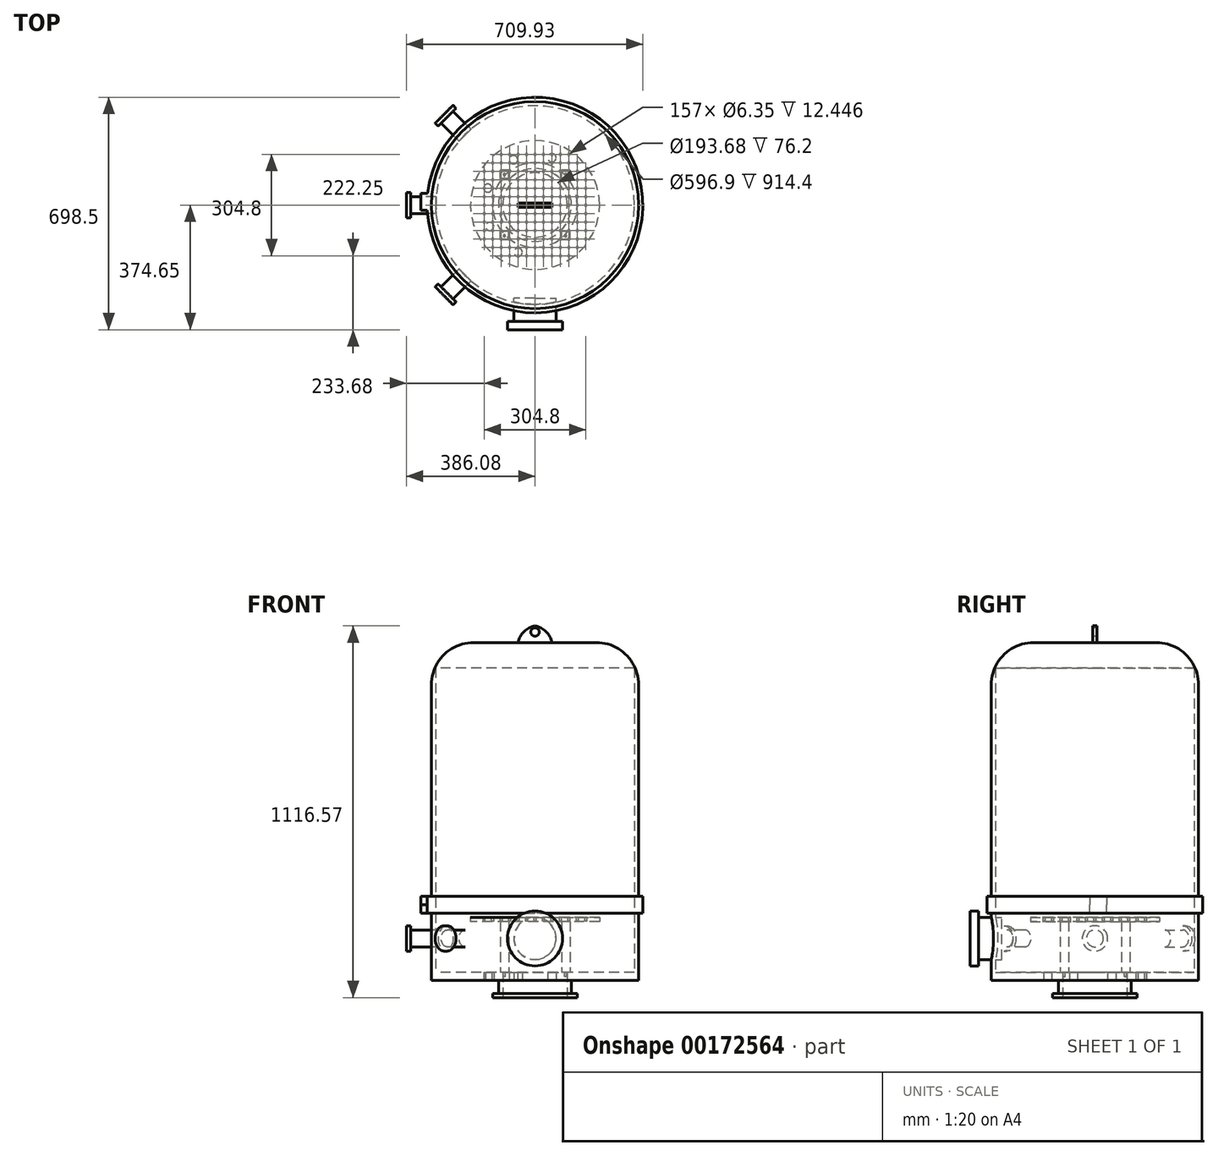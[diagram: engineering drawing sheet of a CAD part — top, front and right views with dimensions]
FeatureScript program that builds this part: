
annotation { "Feature Type Name" : "Feature", "Feature Type Description" : "" }
export const myFeature = defineFeature(function(context is Context, id is Id, definition is map)
    precondition{}
    {
        {
            var Q0;
            Q0=qCreatedBy(makeId("Top.planeOp"),FACE);
            var sketch = newSketch(context, id + "F0", { "sketchPlane" : qUnion([Q0])});
            skCircle(sketch, "E0", {"center": v(0, 0) * mm, "radius": 311.15 * mm});
            skCircle(sketch, "E1", {"center": v(0, 0) * mm, "radius": 298.45 * mm});
            skSolve(sketch);
        }
        {
            var Q0;
            Q0=makeQuery(id+"F0.imprint","IMPRINT",FACE,{"disambiguationData":[TD([[makeQuery(id+"F0.imprint","IMPRINT",EDGE,{"derivedFrom":sQuery(id+"F0.wireOp",EDGE,"E0")}),1.0]])]});
            extrude(context, id + "F1", {"entities" : qUnion([Q0]), "depth" : 177.8 * mm});
        }
        {
            var Q0;
            Q0=makeQuery(id+"F1.opExtrude","CAP_FACE",FACE,{"disambiguationData":[OSD([sQuery(id+"F0.wireOp",EDGE,"E0"),sQuery(id+"F0.wireOp",EDGE,"E1")])],"isStart":false});
            var sketch = newSketch(context, id + "F2", { "sketchPlane" : qUnion([Q0])});
            skCircle(sketch, "E2", {"center": v(0, 0) * mm, "radius": 323.85 * mm});
            skCircle(sketch, "E3", {"center": v(0, 0) * mm, "radius": 298.45 * mm});
            skSolve(sketch);
        }
        {
            var Q0;
            Q0 = qSketchRegion(id + "F2", true);
            extrude(context, id + "F3", {"entities" : qUnion([Q0]), "operationType" : NewBodyOperationType.ADD, "depth" : 25.4 * mm});
        }
        {
            var Q0;
            Q0=qCreatedBy(makeId("Front.planeOp"),FACE);
            cPlane(context, id + "F4", {"entities" : qUnion([Q0]), "cplaneType" : CPlaneType.OFFSET, "offset" : 304.8 * mm, "width" : 152.4 * mm, "height" : 152.4 * mm});
        }
        {
            var Q0;
            Q0=qCreatedBy(id+"F4.planeOp",FACE);
            var sketch = newSketch(context, id + "F5", { "sketchPlane" : qUnion([Q0])});
            skLineSegment(sketch, "E4", {"start": v(0, 0) * mm, "end": v(0, 203.2) * mm, "construction": true});
            skLineSegment(sketch, "E5", {"start": v(0, 101.6) * mm, "end": v(254, 101.6) * mm, "construction": true});
            skPoint(sketch, "E5.endSnap0", {"position": v(0, 101.6) * mm});
            skLineSegment(sketch, "E6", {"start": v(254, 101.6) * mm, "end": v(-254, 101.6) * mm, "construction": true});
            skCircle(sketch, "E7", {"center": v(0, 101.6) * mm, "radius": 63.5 * mm});
            skSolve(sketch);
        }
        {
            var Q0;
            Q0 = qSketchRegion(id + "F5", true);
            extrude(context, id + "F6", {"entities" : qUnion([Q0]), "operationType" : NewBodyOperationType.ADD, "depth" : 44.45 * mm, "hasSecondDirection" : true, "secondDirectionOppositeDirection" : true, "secondDirectionDepth" : 25.4 * mm});
        }
        {
            var Q0;
            Q0=makeQuery(id+"F6.opExtrude","CAP_FACE",FACE,{"disambiguationData":[OSD([sQuery(id+"F5.wireOp",EDGE,"E7")])],"isStart":false});
            var sketch = newSketch(context, id + "F7", { "sketchPlane" : qUnion([Q0])});
            skCircle(sketch, "E8", {"center": v(0, 101.6) * mm, "radius": 82.55 * mm});
            skSolve(sketch);
        }
        {
            var Q0;
            Q0 = qSketchRegion(id + "F7", true);
            extrude(context, id + "F8", {"entities" : qUnion([Q0]), "operationType" : NewBodyOperationType.ADD, "depth" : 25.4 * mm});
        }
        {
            var Q0;
            Q0=qCreatedBy(makeId("Right.planeOp"),FACE);
            cPlane(context, id + "F9", {"entities" : qUnion([Q0]), "cplaneType" : CPlaneType.OFFSET, "offset" : 304.8 * mm, "oppositeDirection" : true, "width" : 152.4 * mm, "height" : 152.4 * mm});
        }
        {
            var Q0;
            Q0=qCreatedBy(id+"F9.planeOp",FACE);
            var sketch = newSketch(context, id + "F10", { "sketchPlane" : qUnion([Q0])});
            skLineSegment(sketch, "E9", {"start": v(0, 0) * mm, "end": v(0, 203.2) * mm, "construction": true});
            skLineSegment(sketch, "E10", {"start": v(0, 101.6) * mm, "end": v(-254, 101.6) * mm, "construction": true});
            skPoint(sketch, "E10.endSnap0", {"position": v(0, 101.6) * mm});
            skLineSegment(sketch, "E11", {"start": v(-254, 101.6) * mm, "end": v(254, 101.6) * mm, "construction": true});
            skCircle(sketch, "E12", {"center": v(0, 101.6) * mm, "radius": 25.4 * mm});
            skSolve(sketch);
        }
        {
            var Q0;
            Q0 = qSketchRegion(id + "F10", true);
            extrude(context, id + "F11", {"entities" : qUnion([Q0]), "depth" : 7.62 * mm, "hasSecondDirection" : true, "secondDirectionOppositeDirection" : true, "secondDirectionDepth" : 68.58 * mm});
        }
        {
            var Q0;
            Q0=makeQuery(id+"F11.opExtrude","CAP_FACE",FACE,{"disambiguationData":[OSD([sQuery(id+"F10.wireOp",EDGE,"E12")])],"isStart":true});
            var sketch = newSketch(context, id + "F12", { "sketchPlane" : qUnion([Q0])});
            skCircle(sketch, "E13", {"center": v(0, 101.6) * mm, "radius": 38.1 * mm});
            skSolve(sketch);
        }
        {
            var Q0;
            Q0 = qSketchRegion(id + "F12", true);
            extrude(context, id + "F13", {"entities" : qUnion([Q0]), "operationType" : NewBodyOperationType.ADD, "depth" : 12.7 * mm});
        }
        {
            var Q0;
            Q0=makeQuery(id+"F11.opExtrude","SWEPT_BODY",BODY,{"disambiguationData":[OSD([sQuery(id+"F10.wireOp",EDGE,"E12")])]});
            var Q1;
            Q1=makeQuery(id+"F1.opExtrude","CAP_EDGE",EDGE,{"disambiguationData":[OSD([sQuery(id+"F0.wireOp",EDGE,"E0")])],"isStart":true});
            circularPattern(context, id + "F14", {"entities" : qUnion([Q0]), "axis" : qUnion([Q1]), "angle" : 45 * degree, "instanceCount" : 2, "oppositeDirection" : true});
        }
        {
            var Q0;
            Q0=makeQuery(id+"F11.opExtrude","SWEPT_BODY",BODY,{"disambiguationData":[OSD([sQuery(id+"F10.wireOp",EDGE,"E12")])]});
            var Q1;
            Q1=makeQuery(id+"F1.opExtrude","CAP_EDGE",EDGE,{"disambiguationData":[OSD([sQuery(id+"F0.wireOp",EDGE,"E0")])],"isStart":true});
            circularPattern(context, id + "F15", {"entities" : qUnion([Q0]), "axis" : qUnion([Q1]), "angle" : 45 * degree, "instanceCount" : 2});
        }
        {
            var Q0;
            Q0=makeQuery(id+"F3.opExtrude","CAP_FACE",FACE,{"disambiguationData":[OSD([sQuery(id+"F2.wireOp",EDGE,"E2"),sQuery(id+"F2.wireOp",EDGE,"E3")])],"isStart":false});
            var sketch = newSketch(context, id + "F16", { "sketchPlane" : qUnion([Q0])});
            skCircle(sketch, "E14", {"center": v(0, 0) * mm, "radius": 323.85 * mm});
            skCircle(sketch, "E15", {"center": v(0, 0) * mm, "radius": 298.45 * mm});
            skSolve(sketch);
        }
        {
            var Q0;
            Q0 = qSketchRegion(id + "F16", true);
            extrude(context, id + "F17", {"entities" : qUnion([Q0]), "depth" : 25.4 * mm});
        }
        {
            var Q0;
            Q0=makeQuery(id+"F17.opExtrude","CAP_FACE",FACE,{"disambiguationData":[OSD([sQuery(id+"F16.wireOp",EDGE,"E14"),sQuery(id+"F16.wireOp",EDGE,"E15")])],"isStart":false});
            var sketch = newSketch(context, id + "F18", { "sketchPlane" : qUnion([Q0])});
            skCircle(sketch, "E16", {"center": v(0, 0) * mm, "radius": 298.45 * mm});
            skCircle(sketch, "E17", {"center": v(0, 0) * mm, "radius": 311.15 * mm});
            skSolve(sketch);
        }
        {
            var Q0;
            Q0=makeQuery(id+"F18.imprint","IMPRINT",FACE,{"disambiguationData":[TD([[makeQuery(id+"F18.imprint","IMPRINT",EDGE,{"derivedFrom":sQuery(id+"F18.wireOp",EDGE,"E16")}),-1.0]])]});
            extrude(context, id + "F19", {"entities" : qUnion([Q0]), "operationType" : NewBodyOperationType.ADD, "depth" : 685.8 * mm});
        }
        {
            var Q0;
            Q0=makeQuery(id+"F19.opExtrude","CAP_FACE",FACE,{"disambiguationData":[OSD([sQuery(id+"F18.wireOp",EDGE,"0rSFMXk0-wgXn-WOUg-yUmk-ADJ3Ojx0R6x5"),sQuery(id+"F18.wireOp",EDGE,"E16")])],"isStart":false});
            var sketch = newSketch(context, id + "F20", { "sketchPlane" : qUnion([Q0])});
            skCircle(sketch, "E18", {"center": v(0, 0) * mm, "radius": 311.15 * mm});
            skSolve(sketch);
        }
        {
            var Q0;
            Q0 = qSketchRegion(id + "F20", true);
            extrude(context, id + "F21", {"entities" : qUnion([Q0]), "operationType" : NewBodyOperationType.ADD, "depth" : 76.2 * mm});
        }
        {
            var Q0;
            Q0=makeQuery(id+"F1.opExtrude","CAP_FACE",FACE,{"disambiguationData":[OSD([sQuery(id+"F0.wireOp",EDGE,"E0")])],"isStart":true});
            var sketch = newSketch(context, id + "F22", { "sketchPlane" : qUnion([Q0])});
            skCircle(sketch, "E19", {"center": v(0, 0) * mm, "radius": 109.54 * mm});
            skSolve(sketch);
        }
        {
            var Q0;
            Q0 = qSketchRegion(id + "F22", true);
            extrude(context, id + "F23", {"entities" : qUnion([Q0]), "operationType" : NewBodyOperationType.ADD, "depth" : 63.5 * mm});
        }
        {
            var Q0;
            Q0=makeQuery(id+"F1.opExtrude","CAP_FACE",FACE,{"disambiguationData":[OSD([sQuery(id+"F0.wireOp",EDGE,"E0")])],"isStart":true});
            var sketch = newSketch(context, id + "F24", { "sketchPlane" : qUnion([Q0])});
            skLineSegment(sketch, "E20", {"start": v(50.72, -141.82) * mm, "end": v(0, 0) * mm, "construction": true});
            skCircle(sketch, "E21", {"center": v(50.72, -141.82) * mm, "radius": 12.5 * mm});
            skCircle(sketch, "E22.1.0", {"center": v(-64.42, -136.14) * mm, "radius": 12.5 * mm});
            skCircle(sketch, "E22.2.0", {"center": v(-141.82, -50.72) * mm, "radius": 12.5 * mm});
            skCircle(sketch, "E22.3.0", {"center": v(-136.14, 64.42) * mm, "radius": 12.5 * mm});
            skCircle(sketch, "E22.4.0", {"center": v(-50.72, 141.82) * mm, "radius": 12.5 * mm});
            skPoint(sketch, "E22.center", {"position": v(0, 0) * mm});
            skLineSegment(sketch, "E22.anchor2", {"start": v(-50.72, 141.82) * mm, "end": v(0, 0) * mm, "construction": true});
            skCircle(sketch, "E23", {"center": v(0, 0) * mm, "radius": 96.84 * mm});
            skSolve(sketch);
        }
        {
            var Q0;
            Q0=makeQuery(id+"F21.opExtrude","CAP_FACE",FACE,{"disambiguationData":[OSD([sQuery(id+"F20.wireOp",EDGE,"E18")])],"isStart":false});
            var sketch = newSketch(context, id + "F25", { "sketchPlane" : qUnion([Q0])});
            skPoint(sketch, "E24.0.midPoint", {"position": v(0, 0) * mm});
            skLineSegment(sketch, "E25.bottom", {"start": v(50.8, -6.35) * mm, "end": v(-50.8, -6.35) * mm});
            skLineSegment(sketch, "E25.top", {"start": v(50.8, 6.35) * mm, "end": v(-50.8, 6.35) * mm});
            skLineSegment(sketch, "E25.left", {"start": v(50.8, -6.35) * mm, "end": v(50.8, 6.35) * mm});
            skLineSegment(sketch, "E25.right", {"start": v(-50.8, -6.35) * mm, "end": v(-50.8, 6.35) * mm});
            skSolve(sketch);
        }
        {
            var Q0;
            Q0=makeQuery(id+"F25.imprint","IMPRINT",FACE,{"disambiguationData":[TD([[makeQuery(id+"F25.imprint","IMPRINT",EDGE,{"derivedFrom":sQuery(id+"F25.wireOp",EDGE,"E25.bottom")}),-1.0]])]});
            extrude(context, id + "F26", {"entities" : qUnion([Q0]), "operationType" : NewBodyOperationType.ADD, "depth" : 50.8 * mm});
        }
        {
            var Q0;
            Q0=makeQuery(id+"F26.opExtrude","SWEPT_FACE",FACE,{"disambiguationData":[OSD([sQuery(id+"F25.wireOp",EDGE,"E25.bottom")])]});
            var sketch = newSketch(context, id + "F27", { "sketchPlane" : qUnion([Q0])});
            skLineSegment(sketch, "E26", {"start": v(0, 1041.4) * mm, "end": v(0, 990.6) * mm, "construction": true});
            skLineSegment(sketch, "E27", {"start": v(50.8, 1016) * mm, "end": v(-50.8, 1016) * mm, "construction": true});
            skLineSegment(sketch, "E28", {"start": v(0, 1041.4) * mm, "end": v(0, 1022.35) * mm, "construction": true});
            skCircle(sketch, "E29", {"center": v(0, 1022.35) * mm, "radius": 12.7 * mm});
            skSolve(sketch);
        }
        {
            var Q0;
            Q0=makeQuery(id+"F26.opExtrude","CAP_EDGE",EDGE,{"disambiguationData":[OSD([sQuery(id+"F25.wireOp",EDGE,"E25.left")])],"isStart":false});
            var Q1;
            Q1=makeQuery(id+"F26.opExtrude","CAP_EDGE",EDGE,{"disambiguationData":[OSD([sQuery(id+"F25.wireOp",EDGE,"E25.right")])],"isStart":false});
            fillet(context, id + "F28", {"entities" : qUnion([Q0, Q1]), "radius" : 63.5 * mm, "tangentPropagation" : true, "allowEdgeOverflow" : false});
        }
        {
            var Q0;
            Q0=makeQuery(id+"F21.opExtrude","CAP_EDGE",EDGE,{"disambiguationData":[OSD([sQuery(id+"F20.wireOp",EDGE,"E18")])],"isStart":false});
            fillet(context, id + "F29", {"entities" : qUnion([Q0]), "radius" : 127 * mm, "tangentPropagation" : true, "allowEdgeOverflow" : false});
        }
        {
            var Q0;
            Q0=qCreatedBy(id+"F9.planeOp",FACE);
            cPlane(context, id + "F30", {"entities" : qUnion([Q0]), "cplaneType" : CPlaneType.OFFSET, "offset" : 38.1 * mm, "oppositeDirection" : true, "width" : 152.4 * mm, "height" : 152.4 * mm});
        }
        {
            var Q0;
            Q0=qCreatedBy(id+"F30.planeOp",FACE);
            var sketch = newSketch(context, id + "F31", { "sketchPlane" : qUnion([Q0])});
            skLineSegment(sketch, "E30.bottom", {"start": v(34.48, 203.2) * mm, "end": v(-16.32, 203.2) * mm});
            skLineSegment(sketch, "E30.top", {"start": v(34.48, 177.8) * mm, "end": v(-16.32, 177.8) * mm});
            skLineSegment(sketch, "E30.left", {"start": v(34.48, 203.2) * mm, "end": v(34.48, 177.8) * mm});
            skLineSegment(sketch, "E30.right", {"start": v(-16.32, 203.2) * mm, "end": v(-16.32, 177.8) * mm});
            skSolve(sketch);
        }
        {
            var Q0;
            Q0 = qSketchRegion(id + "F31", true);
            extrude(context, id + "F32", {"entities" : qUnion([Q0]), "operationType" : NewBodyOperationType.ADD, "depth" : 25.4 * mm});
        }
        {
            var Q0;
            Q0=qCreatedBy(id+"F30.planeOp",FACE);
            var sketch = newSketch(context, id + "F33", { "sketchPlane" : qUnion([Q0])});
            skLineSegment(sketch, "E31.bottom", {"start": v(35.05, 203.2) * mm, "end": v(-15.75, 203.2) * mm});
            skLineSegment(sketch, "E31.top", {"start": v(35.05, 228.6) * mm, "end": v(-15.75, 228.6) * mm});
            skLineSegment(sketch, "E31.left", {"start": v(35.05, 203.2) * mm, "end": v(35.05, 228.6) * mm});
            skLineSegment(sketch, "E31.right", {"start": v(-15.75, 203.2) * mm, "end": v(-15.75, 228.6) * mm});
            skSolve(sketch);
        }
        {
            var Q0;
            Q0 = qSketchRegion(id + "F33", true);
            extrude(context, id + "F34", {"entities" : qUnion([Q0]), "operationType" : NewBodyOperationType.ADD, "depth" : 25.4 * mm});
        }
        {
            var Q0;
            Q0=makeQuery(id+"F1.opExtrude","CAP_FACE",FACE,{"disambiguationData":[OSD([sQuery(id+"F0.wireOp",EDGE,"E0"),sQuery(id+"F0.wireOp",EDGE,"E1")])],"isStart":true});
            var sketch = newSketch(context, id + "F35", { "sketchPlane" : qUnion([Q0])});
            skCircle(sketch, "E32", {"center": v(0, 0) * mm, "radius": 311.15 * mm});
            skSolve(sketch);
        }
        {
            var Q0;
            Q0 = qSketchRegion(id + "F35", true);
            extrude(context, id + "F36", {"entities" : qUnion([Q0]), "operationType" : NewBodyOperationType.ADD, "depth" : 25 * mm});
        }
        {
            var Q0;
            Q0=makeQuery(id+"F27.imprint","IMPRINT",FACE,{"disambiguationData":[TD([[makeQuery(id+"F27.imprint","IMPRINT",EDGE,{"derivedFrom":sQuery(id+"F27.wireOp",EDGE,"E29")}),1.0]])]});
            var Q1;
            Q1=sQuery(id+"F27.wireOp",EDGE,"E29");
            extrude(context, id + "F37", {"entities" : qUnion([Q0]), "operationType" : NewBodyOperationType.REMOVE, "surfaceEntities" : qUnion([Q1]), "oppositeDirection" : true, "depth" : 25.4 * mm, "hasSecondDirection" : true, "secondDirectionOppositeDirection" : false, "secondDirectionDepth" : 25.4 * mm});
        }
        {
            var Q0;
            Q0=makeQuery(id+"F23.opExtrude","CAP_FACE",FACE,{"disambiguationData":[OSD([sQuery(id+"F22.wireOp",EDGE,"E19")])],"isStart":false});
            var sketch = newSketch(context, id + "F38", { "sketchPlane" : qUnion([Q0])});
            skCircle(sketch, "E33", {"center": v(0, 0) * mm, "radius": 127 * mm});
            skSolve(sketch);
        }
        {
            var Q0;
            Q0 = qSketchRegion(id + "F38", true);
            extrude(context, id + "F39", {"entities" : qUnion([Q0]), "operationType" : NewBodyOperationType.ADD, "depth" : 12.7 * mm});
        }
        {
            var Q0;
            Q0 = qSketchRegion(id + "F24", true);
            extrude(context, id + "F40", {"entities" : qUnion([Q0]), "operationType" : NewBodyOperationType.REMOVE, "oppositeDirection" : true, "depth" : 254 * mm, "hasSecondDirection" : true, "secondDirectionOppositeDirection" : false, "secondDirectionDepth" : 254 * mm});
        }
        {
            var Q0;
            Q0=makeQuery(id+"F36.boolean.opBoolean","MERGE",FACE,{"derivedFrom":[makeQuery(id+"F23.opExtrude","CAP_FACE",FACE,{"disambiguationData":[OSD([sQuery(id+"F22.wireOp",EDGE,"E19")])],"isStart":true}),makeQuery(id+"F36.opExtrude","CAP_FACE",FACE,{"disambiguationData":[OSD([sQuery(id+"F35.wireOp",EDGE,"E32")])],"isStart":true})]});
            var sketch = newSketch(context, id + "F41", { "sketchPlane" : qUnion([Q0])});
            skLineSegment(sketch, "E34.bottom", {"start": v(101.6, -101.6) * mm, "end": v(-101.6, -101.6) * mm, "construction": true});
            skLineSegment(sketch, "E34.top", {"start": v(101.6, 101.6) * mm, "end": v(-101.6, 101.6) * mm, "construction": true});
            skLineSegment(sketch, "E34.left", {"start": v(101.6, -101.6) * mm, "end": v(101.6, 101.6) * mm, "construction": true});
            skLineSegment(sketch, "E34.right", {"start": v(-101.6, -101.6) * mm, "end": v(-101.6, 101.6) * mm, "construction": true});
            skPoint(sketch, "E34.middle", {"position": v(0, 0) * mm});
            skLineSegment(sketch, "E35.bottom", {"start": v(-101.6, 101.6) * mm, "end": v(-92.07, 101.6) * mm, "construction": true});
            skLineSegment(sketch, "E35.top", {"start": v(-101.6, 92.08) * mm, "end": v(-92.07, 92.08) * mm, "construction": true});
            skLineSegment(sketch, "E35.left", {"start": v(-101.6, 101.6) * mm, "end": v(-101.6, 92.08) * mm, "construction": true});
            skLineSegment(sketch, "E35.right", {"start": v(-92.07, 101.6) * mm, "end": v(-92.07, 92.08) * mm, "construction": true});
            skLineSegment(sketch, "E36.0.1.0", {"start": v(-92.07, -82.55) * mm, "end": v(-92.07, -92.07) * mm, "construction": true});
            skLineSegment(sketch, "E36.1.0.0", {"start": v(92.08, 101.6) * mm, "end": v(92.08, 92.08) * mm, "construction": true});
            skLineSegment(sketch, "E36.1.1.0", {"start": v(92.08, -82.55) * mm, "end": v(92.08, -92.08) * mm, "construction": true});
            skLineSegment(sketch, "E36.direction1", {"start": v(-92.07, 92.08) * mm, "end": v(92.08, 92.08) * mm, "construction": true});
            skLineSegment(sketch, "E36.direction2", {"start": v(-92.07, 92.08) * mm, "end": v(-92.07, -92.07) * mm, "construction": true});
            skCircle(sketch, "E37", {"center": v(-92.07, 92.08) * mm, "radius": 3.18 * mm});
            skCircle(sketch, "E38", {"center": v(92.08, 92.08) * mm, "radius": 3.18 * mm});
            skCircle(sketch, "E39", {"center": v(92.08, -92.08) * mm, "radius": 3.18 * mm});
            skCircle(sketch, "E40", {"center": v(-92.07, -92.07) * mm, "radius": 3.18 * mm});
            skSolve(sketch);
        }
        {
            var Q0;
            Q0 = qSketchRegion(id + "F41", true);
            extrude(context, id + "F42", {"entities" : qUnion([Q0]), "operationType" : NewBodyOperationType.REMOVE, "oppositeDirection" : true, "depth" : 12.7 * mm});
        }
        {
            var Q0;
            Q0=makeQuery(id+"F36.boolean.opBoolean","MERGE",FACE,{"derivedFrom":[makeQuery(id+"F23.opExtrude","CAP_FACE",FACE,{"disambiguationData":[OSD([sQuery(id+"F22.wireOp",EDGE,"E19")])],"isStart":true}),makeQuery(id+"F36.opExtrude","CAP_FACE",FACE,{"disambiguationData":[OSD([sQuery(id+"F35.wireOp",EDGE,"E32")])],"isStart":true})]});
            var sketch = newSketch(context, id + "F43", { "sketchPlane" : qUnion([Q0])});
            skLineSegment(sketch, "E41.bottom", {"start": v(-79.37, 79.38) * mm, "end": v(-104.77, 79.38) * mm});
            skLineSegment(sketch, "E41.top", {"start": v(-79.37, 104.78) * mm, "end": v(-104.77, 104.78) * mm});
            skLineSegment(sketch, "E41.left", {"start": v(-79.37, 79.38) * mm, "end": v(-79.37, 104.78) * mm});
            skLineSegment(sketch, "E41.right", {"start": v(-104.77, 79.38) * mm, "end": v(-104.77, 104.78) * mm});
            skPoint(sketch, "E41.middle", {"position": v(-92.07, 92.08) * mm});
            skLineSegment(sketch, "E42.bottom", {"start": v(104.78, 79.38) * mm, "end": v(79.38, 79.38) * mm});
            skLineSegment(sketch, "E42.top", {"start": v(104.78, 104.77) * mm, "end": v(79.38, 104.77) * mm});
            skLineSegment(sketch, "E42.left", {"start": v(104.78, 79.38) * mm, "end": v(104.78, 104.77) * mm});
            skLineSegment(sketch, "E42.right", {"start": v(79.38, 79.38) * mm, "end": v(79.38, 104.77) * mm});
            skPoint(sketch, "E42.middle", {"position": v(92.08, 92.08) * mm});
            skLineSegment(sketch, "E43.bottom", {"start": v(104.78, -104.78) * mm, "end": v(79.38, -104.78) * mm});
            skLineSegment(sketch, "E43.top", {"start": v(104.78, -79.38) * mm, "end": v(79.38, -79.38) * mm});
            skLineSegment(sketch, "E43.left", {"start": v(104.78, -104.78) * mm, "end": v(104.78, -79.38) * mm});
            skLineSegment(sketch, "E43.right", {"start": v(79.38, -104.78) * mm, "end": v(79.38, -79.38) * mm});
            skPoint(sketch, "E43.middle", {"position": v(92.08, -92.08) * mm});
            skLineSegment(sketch, "E44.bottom", {"start": v(-79.37, -104.77) * mm, "end": v(-104.77, -104.77) * mm});
            skLineSegment(sketch, "E44.top", {"start": v(-79.37, -79.37) * mm, "end": v(-104.77, -79.37) * mm});
            skLineSegment(sketch, "E44.left", {"start": v(-79.37, -104.77) * mm, "end": v(-79.37, -79.37) * mm});
            skLineSegment(sketch, "E44.right", {"start": v(-104.77, -104.77) * mm, "end": v(-104.77, -79.37) * mm});
            skPoint(sketch, "E44.middle", {"position": v(-92.07, -92.07) * mm});
            skSolve(sketch);
        }
        {
            var Q0;
            Q0 = qSketchRegion(id + "F43", true);
            extrude(context, id + "F44", {"entities" : qUnion([Q0]), "depth" : 152.4 * mm});
        }
        {
            var Q0;
            Q0=makeQuery(id+"F44.opExtrude","CAP_FACE",FACE,{"disambiguationData":[OSD([sQuery(id+"F43.wireOp",EDGE,"E41.bottom"),sQuery(id+"F43.wireOp",EDGE,"E41.top"),sQuery(id+"F43.wireOp",EDGE,"E41.left"),sQuery(id+"F43.wireOp",EDGE,"E41.right")])],"isStart":false});
            var sketch = newSketch(context, id + "F45", { "sketchPlane" : qUnion([Q0])});
            skCircle(sketch, "E45", {"center": v(0, 0) * mm, "radius": 193.67 * mm});
            skSolve(sketch);
        }
        {
            var Q0;
            Q0 = qSketchRegion(id + "F45", true);
            extrude(context, id + "F46", {"entities" : qUnion([Q0]), "operationType" : NewBodyOperationType.ADD, "depth" : 12.7 * mm});
        }
        {
            var Q0;
            Q0=makeQuery(id+"F46.opExtrude","CAP_FACE",FACE,{"disambiguationData":[OSD([sQuery(id+"F45.wireOp",EDGE,"E45")])],"isStart":false});
            var sketch = newSketch(context, id + "F47", { "sketchPlane" : qUnion([Q0])});
            skCircle(sketch, "E46", {"center": v(0, 0) * mm, "radius": 3.18 * mm});
            skCircle(sketch, "E47.0.1.0", {"center": v(0, 25.4) * mm, "radius": 3.18 * mm});
            skCircle(sketch, "E47.0.2.0", {"center": v(0, 50.8) * mm, "radius": 3.18 * mm});
            skCircle(sketch, "E47.0.3.0", {"center": v(0, 76.2) * mm, "radius": 3.18 * mm});
            skCircle(sketch, "E47.0.4.0", {"center": v(0, 101.6) * mm, "radius": 3.18 * mm});
            skCircle(sketch, "E47.0.5.0", {"center": v(0, 127) * mm, "radius": 3.18 * mm});
            skCircle(sketch, "E47.0.6.0", {"center": v(0, 152.4) * mm, "radius": 3.18 * mm});
            skCircle(sketch, "E47.1.0.0", {"center": v(25.4, 0) * mm, "radius": 3.18 * mm});
            skCircle(sketch, "E47.1.1.0", {"center": v(25.4, 25.4) * mm, "radius": 3.18 * mm});
            skCircle(sketch, "E47.1.2.0", {"center": v(25.4, 50.8) * mm, "radius": 3.18 * mm});
            skCircle(sketch, "E47.1.3.0", {"center": v(25.4, 76.2) * mm, "radius": 3.18 * mm});
            skCircle(sketch, "E47.1.4.0", {"center": v(25.4, 101.6) * mm, "radius": 3.18 * mm});
            skCircle(sketch, "E47.1.5.0", {"center": v(25.4, 127) * mm, "radius": 3.18 * mm});
            skCircle(sketch, "E47.1.6.0", {"center": v(25.4, 152.4) * mm, "radius": 3.18 * mm});
            skCircle(sketch, "E47.2.0.0", {"center": v(50.8, 0) * mm, "radius": 3.18 * mm});
            skCircle(sketch, "E47.2.1.0", {"center": v(50.8, 25.4) * mm, "radius": 3.18 * mm});
            skCircle(sketch, "E47.2.2.0", {"center": v(50.8, 50.8) * mm, "radius": 3.18 * mm});
            skCircle(sketch, "E47.2.3.0", {"center": v(50.8, 76.2) * mm, "radius": 3.18 * mm});
            skCircle(sketch, "E47.2.4.0", {"center": v(50.8, 101.6) * mm, "radius": 3.18 * mm});
            skCircle(sketch, "E47.2.5.0", {"center": v(50.8, 127) * mm, "radius": 3.18 * mm});
            skCircle(sketch, "E47.2.6.0", {"center": v(50.8, 152.4) * mm, "radius": 3.18 * mm});
            skCircle(sketch, "E47.3.0.0", {"center": v(76.2, 0) * mm, "radius": 3.18 * mm});
            skCircle(sketch, "E47.3.1.0", {"center": v(76.2, 25.4) * mm, "radius": 3.18 * mm});
            skCircle(sketch, "E47.3.2.0", {"center": v(76.2, 50.8) * mm, "radius": 3.18 * mm});
            skCircle(sketch, "E47.3.3.0", {"center": v(76.2, 76.2) * mm, "radius": 3.18 * mm});
            skCircle(sketch, "E47.3.4.0", {"center": v(76.2, 101.6) * mm, "radius": 3.18 * mm});
            skCircle(sketch, "E47.3.5.0", {"center": v(76.2, 127) * mm, "radius": 3.18 * mm});
            skCircle(sketch, "E47.3.6.0", {"center": v(76.2, 152.4) * mm, "radius": 3.18 * mm});
            skCircle(sketch, "E47.4.0.0", {"center": v(101.6, 0) * mm, "radius": 3.18 * mm});
            skCircle(sketch, "E47.4.1.0", {"center": v(101.6, 25.4) * mm, "radius": 3.18 * mm});
            skCircle(sketch, "E47.4.2.0", {"center": v(101.6, 50.8) * mm, "radius": 3.18 * mm});
            skCircle(sketch, "E47.4.3.0", {"center": v(101.6, 76.2) * mm, "radius": 3.18 * mm});
            skCircle(sketch, "E47.4.4.0", {"center": v(101.6, 101.6) * mm, "radius": 3.18 * mm});
            skCircle(sketch, "E47.4.5.0", {"center": v(101.6, 127) * mm, "radius": 3.18 * mm});
            skCircle(sketch, "E47.4.6.0", {"center": v(101.6, 152.4) * mm, "radius": 3.18 * mm});
            skCircle(sketch, "E47.5.0.0", {"center": v(127, 0) * mm, "radius": 3.18 * mm});
            skCircle(sketch, "E47.5.1.0", {"center": v(127, 25.4) * mm, "radius": 3.18 * mm});
            skCircle(sketch, "E47.5.2.0", {"center": v(127, 50.8) * mm, "radius": 3.18 * mm});
            skCircle(sketch, "E47.5.3.0", {"center": v(127, 76.2) * mm, "radius": 3.18 * mm});
            skCircle(sketch, "E47.5.4.0", {"center": v(127, 101.6) * mm, "radius": 3.18 * mm});
            skCircle(sketch, "E47.5.5.0", {"center": v(127, 127) * mm, "radius": 3.18 * mm});
            skCircle(sketch, "E47.5.6.0", {"center": v(127, 152.4) * mm, "radius": 3.18 * mm});
            skCircle(sketch, "E47.6.0.0", {"center": v(152.4, 0) * mm, "radius": 3.18 * mm});
            skCircle(sketch, "E47.6.1.0", {"center": v(152.4, 25.4) * mm, "radius": 3.18 * mm});
            skCircle(sketch, "E47.6.2.0", {"center": v(152.4, 50.8) * mm, "radius": 3.18 * mm});
            skCircle(sketch, "E47.6.3.0", {"center": v(152.4, 76.2) * mm, "radius": 3.18 * mm});
            skCircle(sketch, "E47.6.4.0", {"center": v(152.4, 101.6) * mm, "radius": 3.18 * mm});
            skCircle(sketch, "E47.6.5.0", {"center": v(152.4, 127) * mm, "radius": 3.18 * mm});
            skCircle(sketch, "E47.6.6.0", {"center": v(152.4, 152.4) * mm, "radius": 3.18 * mm});
            skLineSegment(sketch, "E47.direction1", {"start": v(0, 0) * mm, "end": v(25.4, 0) * mm, "construction": true});
            skLineSegment(sketch, "E47.direction2", {"start": v(0, 0) * mm, "end": v(0, 25.4) * mm, "construction": true});
            skCircle(sketch, "E48.1.0.0", {"center": v(-25.4, 0) * mm, "radius": 3.18 * mm});
            skCircle(sketch, "E48.1.1.0", {"center": v(-25.4, 25.4) * mm, "radius": 3.18 * mm});
            skCircle(sketch, "E48.1.2.0", {"center": v(-25.4, 50.8) * mm, "radius": 3.18 * mm});
            skCircle(sketch, "E48.1.3.0", {"center": v(-25.4, 76.2) * mm, "radius": 3.18 * mm});
            skCircle(sketch, "E48.1.4.0", {"center": v(-25.4, 101.6) * mm, "radius": 3.18 * mm});
            skCircle(sketch, "E48.1.5.0", {"center": v(-25.4, 127) * mm, "radius": 3.18 * mm});
            skCircle(sketch, "E48.1.6.0", {"center": v(-25.4, 152.4) * mm, "radius": 3.18 * mm});
            skCircle(sketch, "E48.2.0.0", {"center": v(-50.8, 0) * mm, "radius": 3.18 * mm});
            skCircle(sketch, "E48.2.1.0", {"center": v(-50.8, 25.4) * mm, "radius": 3.18 * mm});
            skCircle(sketch, "E48.2.2.0", {"center": v(-50.8, 50.8) * mm, "radius": 3.18 * mm});
            skCircle(sketch, "E48.2.3.0", {"center": v(-50.8, 76.2) * mm, "radius": 3.18 * mm});
            skCircle(sketch, "E48.2.4.0", {"center": v(-50.8, 101.6) * mm, "radius": 3.18 * mm});
            skCircle(sketch, "E48.2.5.0", {"center": v(-50.8, 127) * mm, "radius": 3.18 * mm});
            skCircle(sketch, "E48.2.6.0", {"center": v(-50.8, 152.4) * mm, "radius": 3.18 * mm});
            skCircle(sketch, "E48.3.0.0", {"center": v(-76.2, 0) * mm, "radius": 3.18 * mm});
            skCircle(sketch, "E48.3.1.0", {"center": v(-76.2, 25.4) * mm, "radius": 3.18 * mm});
            skCircle(sketch, "E48.3.2.0", {"center": v(-76.2, 50.8) * mm, "radius": 3.18 * mm});
            skCircle(sketch, "E48.3.3.0", {"center": v(-76.2, 76.2) * mm, "radius": 3.18 * mm});
            skCircle(sketch, "E48.3.4.0", {"center": v(-76.2, 101.6) * mm, "radius": 3.18 * mm});
            skCircle(sketch, "E48.3.5.0", {"center": v(-76.2, 127) * mm, "radius": 3.18 * mm});
            skCircle(sketch, "E48.3.6.0", {"center": v(-76.2, 152.4) * mm, "radius": 3.18 * mm});
            skCircle(sketch, "E48.4.0.0", {"center": v(-101.6, 0) * mm, "radius": 3.18 * mm});
            skCircle(sketch, "E48.4.1.0", {"center": v(-101.6, 25.4) * mm, "radius": 3.18 * mm});
            skCircle(sketch, "E48.4.2.0", {"center": v(-101.6, 50.8) * mm, "radius": 3.18 * mm});
            skCircle(sketch, "E48.4.3.0", {"center": v(-101.6, 76.2) * mm, "radius": 3.18 * mm});
            skCircle(sketch, "E48.4.4.0", {"center": v(-101.6, 101.6) * mm, "radius": 3.18 * mm});
            skCircle(sketch, "E48.4.5.0", {"center": v(-101.6, 127) * mm, "radius": 3.18 * mm});
            skCircle(sketch, "E48.4.6.0", {"center": v(-101.6, 152.4) * mm, "radius": 3.18 * mm});
            skCircle(sketch, "E48.5.0.0", {"center": v(-127, 0) * mm, "radius": 3.18 * mm});
            skCircle(sketch, "E48.5.1.0", {"center": v(-127, 25.4) * mm, "radius": 3.18 * mm});
            skCircle(sketch, "E48.5.2.0", {"center": v(-127, 50.8) * mm, "radius": 3.18 * mm});
            skCircle(sketch, "E48.5.3.0", {"center": v(-127, 76.2) * mm, "radius": 3.18 * mm});
            skCircle(sketch, "E48.5.4.0", {"center": v(-127, 101.6) * mm, "radius": 3.18 * mm});
            skCircle(sketch, "E48.5.5.0", {"center": v(-127, 127) * mm, "radius": 3.18 * mm});
            skCircle(sketch, "E48.5.6.0", {"center": v(-127, 152.4) * mm, "radius": 3.18 * mm});
            skCircle(sketch, "E48.6.0.0", {"center": v(-152.4, 0) * mm, "radius": 3.18 * mm});
            skCircle(sketch, "E48.6.1.0", {"center": v(-152.4, 25.4) * mm, "radius": 3.18 * mm});
            skCircle(sketch, "E48.6.2.0", {"center": v(-152.4, 50.8) * mm, "radius": 3.18 * mm});
            skCircle(sketch, "E48.6.3.0", {"center": v(-152.4, 76.2) * mm, "radius": 3.18 * mm});
            skCircle(sketch, "E48.6.4.0", {"center": v(-152.4, 101.6) * mm, "radius": 3.18 * mm});
            skCircle(sketch, "E48.6.5.0", {"center": v(-152.4, 127) * mm, "radius": 3.18 * mm});
            skCircle(sketch, "E48.6.6.0", {"center": v(-152.4, 152.4) * mm, "radius": 3.18 * mm});
            skLineSegment(sketch, "E48.direction1", {"start": v(0, 0) * mm, "end": v(-25.4, 0) * mm, "construction": true});
            skCircle(sketch, "E49.0.1.0", {"center": v(0, -25.4) * mm, "radius": 3.18 * mm});
            skCircle(sketch, "E49.0.2.0", {"center": v(0, -50.8) * mm, "radius": 3.18 * mm});
            skCircle(sketch, "E49.0.3.0", {"center": v(0, -76.2) * mm, "radius": 3.18 * mm});
            skCircle(sketch, "E49.0.4.0", {"center": v(0, -101.6) * mm, "radius": 3.18 * mm});
            skCircle(sketch, "E49.0.5.0", {"center": v(0, -127) * mm, "radius": 3.18 * mm});
            skCircle(sketch, "E49.0.6.0", {"center": v(0, -152.4) * mm, "radius": 3.18 * mm});
            skCircle(sketch, "E49.1.1.0", {"center": v(25.4, -25.4) * mm, "radius": 3.18 * mm});
            skCircle(sketch, "E49.1.2.0", {"center": v(25.4, -50.8) * mm, "radius": 3.18 * mm});
            skCircle(sketch, "E49.1.3.0", {"center": v(25.4, -76.2) * mm, "radius": 3.18 * mm});
            skCircle(sketch, "E49.1.4.0", {"center": v(25.4, -101.6) * mm, "radius": 3.18 * mm});
            skCircle(sketch, "E49.1.5.0", {"center": v(25.4, -127) * mm, "radius": 3.18 * mm});
            skCircle(sketch, "E49.1.6.0", {"center": v(25.4, -152.4) * mm, "radius": 3.18 * mm});
            skCircle(sketch, "E49.2.1.0", {"center": v(50.8, -25.4) * mm, "radius": 3.18 * mm});
            skCircle(sketch, "E49.2.2.0", {"center": v(50.8, -50.8) * mm, "radius": 3.18 * mm});
            skCircle(sketch, "E49.2.3.0", {"center": v(50.8, -76.2) * mm, "radius": 3.18 * mm});
            skCircle(sketch, "E49.2.4.0", {"center": v(50.8, -101.6) * mm, "radius": 3.18 * mm});
            skCircle(sketch, "E49.2.5.0", {"center": v(50.8, -127) * mm, "radius": 3.18 * mm});
            skCircle(sketch, "E49.2.6.0", {"center": v(50.8, -152.4) * mm, "radius": 3.18 * mm});
            skCircle(sketch, "E49.3.1.0", {"center": v(76.2, -25.4) * mm, "radius": 3.18 * mm});
            skCircle(sketch, "E49.3.2.0", {"center": v(76.2, -50.8) * mm, "radius": 3.18 * mm});
            skCircle(sketch, "E49.3.3.0", {"center": v(76.2, -76.2) * mm, "radius": 3.18 * mm});
            skCircle(sketch, "E49.3.4.0", {"center": v(76.2, -101.6) * mm, "radius": 3.18 * mm});
            skCircle(sketch, "E49.3.5.0", {"center": v(76.2, -127) * mm, "radius": 3.18 * mm});
            skCircle(sketch, "E49.3.6.0", {"center": v(76.2, -152.4) * mm, "radius": 3.18 * mm});
            skCircle(sketch, "E49.4.1.0", {"center": v(101.6, -25.4) * mm, "radius": 3.18 * mm});
            skCircle(sketch, "E49.4.2.0", {"center": v(101.6, -50.8) * mm, "radius": 3.18 * mm});
            skCircle(sketch, "E49.4.3.0", {"center": v(101.6, -76.2) * mm, "radius": 3.18 * mm});
            skCircle(sketch, "E49.4.4.0", {"center": v(101.6, -101.6) * mm, "radius": 3.18 * mm});
            skCircle(sketch, "E49.4.5.0", {"center": v(101.6, -127) * mm, "radius": 3.18 * mm});
            skCircle(sketch, "E49.4.6.0", {"center": v(101.6, -152.4) * mm, "radius": 3.18 * mm});
            skCircle(sketch, "E49.5.1.0", {"center": v(127, -25.4) * mm, "radius": 3.18 * mm});
            skCircle(sketch, "E49.5.2.0", {"center": v(127, -50.8) * mm, "radius": 3.18 * mm});
            skCircle(sketch, "E49.5.3.0", {"center": v(127, -76.2) * mm, "radius": 3.18 * mm});
            skCircle(sketch, "E49.5.4.0", {"center": v(127, -101.6) * mm, "radius": 3.18 * mm});
            skCircle(sketch, "E49.5.5.0", {"center": v(127, -127) * mm, "radius": 3.18 * mm});
            skCircle(sketch, "E49.5.6.0", {"center": v(127, -152.4) * mm, "radius": 3.18 * mm});
            skCircle(sketch, "E49.6.1.0", {"center": v(152.4, -25.4) * mm, "radius": 3.18 * mm});
            skCircle(sketch, "E49.6.2.0", {"center": v(152.4, -50.8) * mm, "radius": 3.18 * mm});
            skCircle(sketch, "E49.6.3.0", {"center": v(152.4, -76.2) * mm, "radius": 3.18 * mm});
            skCircle(sketch, "E49.6.4.0", {"center": v(152.4, -101.6) * mm, "radius": 3.18 * mm});
            skCircle(sketch, "E49.6.5.0", {"center": v(152.4, -127) * mm, "radius": 3.18 * mm});
            skCircle(sketch, "E49.6.6.0", {"center": v(152.4, -152.4) * mm, "radius": 3.18 * mm});
            skLineSegment(sketch, "E49.direction2", {"start": v(0, 0) * mm, "end": v(0, -25.4) * mm, "construction": true});
            skCircle(sketch, "E50.1.1.0", {"center": v(-25.4, -25.4) * mm, "radius": 3.18 * mm});
            skCircle(sketch, "E50.1.2.0", {"center": v(-25.4, -50.8) * mm, "radius": 3.18 * mm});
            skCircle(sketch, "E50.1.3.0", {"center": v(-25.4, -76.2) * mm, "radius": 3.18 * mm});
            skCircle(sketch, "E50.1.4.0", {"center": v(-25.4, -101.6) * mm, "radius": 3.18 * mm});
            skCircle(sketch, "E50.1.5.0", {"center": v(-25.4, -127) * mm, "radius": 3.18 * mm});
            skCircle(sketch, "E50.1.6.0", {"center": v(-25.4, -152.4) * mm, "radius": 3.18 * mm});
            skCircle(sketch, "E50.2.1.0", {"center": v(-50.8, -25.4) * mm, "radius": 3.18 * mm});
            skCircle(sketch, "E50.2.2.0", {"center": v(-50.8, -50.8) * mm, "radius": 3.18 * mm});
            skCircle(sketch, "E50.2.3.0", {"center": v(-50.8, -76.2) * mm, "radius": 3.18 * mm});
            skCircle(sketch, "E50.2.4.0", {"center": v(-50.8, -101.6) * mm, "radius": 3.18 * mm});
            skCircle(sketch, "E50.2.5.0", {"center": v(-50.8, -127) * mm, "radius": 3.18 * mm});
            skCircle(sketch, "E50.2.6.0", {"center": v(-50.8, -152.4) * mm, "radius": 3.18 * mm});
            skCircle(sketch, "E50.3.1.0", {"center": v(-76.2, -25.4) * mm, "radius": 3.18 * mm});
            skCircle(sketch, "E50.3.2.0", {"center": v(-76.2, -50.8) * mm, "radius": 3.18 * mm});
            skCircle(sketch, "E50.3.3.0", {"center": v(-76.2, -76.2) * mm, "radius": 3.18 * mm});
            skCircle(sketch, "E50.3.4.0", {"center": v(-76.2, -101.6) * mm, "radius": 3.18 * mm});
            skCircle(sketch, "E50.3.5.0", {"center": v(-76.2, -127) * mm, "radius": 3.18 * mm});
            skCircle(sketch, "E50.3.6.0", {"center": v(-76.2, -152.4) * mm, "radius": 3.18 * mm});
            skCircle(sketch, "E50.4.1.0", {"center": v(-101.6, -25.4) * mm, "radius": 3.18 * mm});
            skCircle(sketch, "E50.4.2.0", {"center": v(-101.6, -50.8) * mm, "radius": 3.18 * mm});
            skCircle(sketch, "E50.4.3.0", {"center": v(-101.6, -76.2) * mm, "radius": 3.18 * mm});
            skCircle(sketch, "E50.4.4.0", {"center": v(-101.6, -101.6) * mm, "radius": 3.18 * mm});
            skCircle(sketch, "E50.4.5.0", {"center": v(-101.6, -127) * mm, "radius": 3.18 * mm});
            skCircle(sketch, "E50.4.6.0", {"center": v(-101.6, -152.4) * mm, "radius": 3.18 * mm});
            skCircle(sketch, "E50.5.1.0", {"center": v(-127, -25.4) * mm, "radius": 3.18 * mm});
            skCircle(sketch, "E50.5.2.0", {"center": v(-127, -50.8) * mm, "radius": 3.18 * mm});
            skCircle(sketch, "E50.5.3.0", {"center": v(-127, -76.2) * mm, "radius": 3.18 * mm});
            skCircle(sketch, "E50.5.4.0", {"center": v(-127, -101.6) * mm, "radius": 3.18 * mm});
            skCircle(sketch, "E50.5.5.0", {"center": v(-127, -127) * mm, "radius": 3.18 * mm});
            skCircle(sketch, "E50.5.6.0", {"center": v(-127, -152.4) * mm, "radius": 3.18 * mm});
            skCircle(sketch, "E50.6.1.0", {"center": v(-152.4, -25.4) * mm, "radius": 3.18 * mm});
            skCircle(sketch, "E50.6.2.0", {"center": v(-152.4, -50.8) * mm, "radius": 3.18 * mm});
            skCircle(sketch, "E50.6.3.0", {"center": v(-152.4, -76.2) * mm, "radius": 3.18 * mm});
            skCircle(sketch, "E50.6.4.0", {"center": v(-152.4, -101.6) * mm, "radius": 3.18 * mm});
            skCircle(sketch, "E50.6.5.0", {"center": v(-152.4, -127) * mm, "radius": 3.18 * mm});
            skCircle(sketch, "E50.6.6.0", {"center": v(-152.4, -152.4) * mm, "radius": 3.18 * mm});
            skSolve(sketch);
        }
        {
            var Q0;
            Q0 = qSketchRegion(id + "F47", true);
            extrude(context, id + "F48", {"entities" : qUnion([Q0]), "operationType" : NewBodyOperationType.REMOVE, "oppositeDirection" : true, "depth" : 12.45 * mm});
        }
    });
